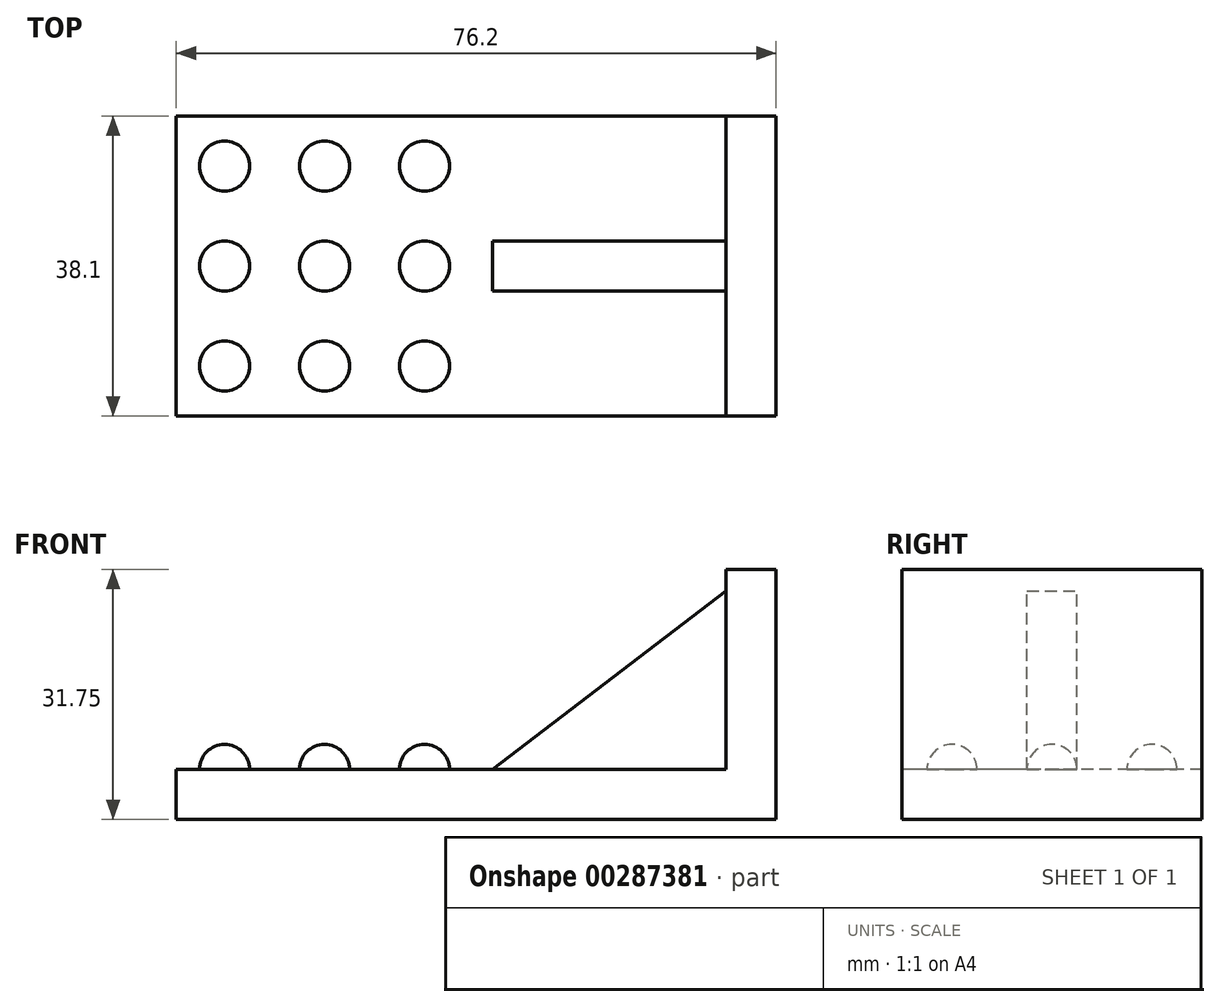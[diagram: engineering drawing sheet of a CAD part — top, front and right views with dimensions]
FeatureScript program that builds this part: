
annotation { "Feature Type Name" : "Feature", "Feature Type Description" : "" }
export const myFeature = defineFeature(function(context is Context, id is Id, definition is map)
    precondition{}
    {
        {
            var Q0;
            Q0=qCreatedBy(makeId("Top.planeOp"),FACE);
            var sketch = newSketch(context, id + "F0", { "sketchPlane" : qUnion([Q0])});
            skLineSegment(sketch, "E0.bottom", {"start": v(-38.1, 19.05) * mm, "end": v(38.1, 19.05) * mm});
            skLineSegment(sketch, "E0.top", {"start": v(-38.1, -19.05) * mm, "end": v(38.1, -19.05) * mm});
            skLineSegment(sketch, "E0.left", {"start": v(-38.1, 19.05) * mm, "end": v(-38.1, -19.05) * mm});
            skLineSegment(sketch, "E0.right", {"start": v(38.1, 19.05) * mm, "end": v(38.1, -19.05) * mm});
            skPoint(sketch, "E0.middle", {"position": v(0, 0) * mm});
            skSolve(sketch);
        }
        {
            var Q0;
            Q0 = qSketchRegion(id + "F0", true);
            extrude(context, id + "F1", {"entities" : qUnion([Q0]), "oppositeDirection" : true, "depth" : 6.35 * mm});
        }
        {
            var Q0;
            Q0=makeQuery(id+"F1.opExtrude","CAP_FACE",FACE,{"disambiguationData":[OSD([sQuery(id+"F0.wireOp",EDGE,"E0.bottom"),sQuery(id+"F0.wireOp",EDGE,"E0.top"),sQuery(id+"F0.wireOp",EDGE,"E0.left"),sQuery(id+"F0.wireOp",EDGE,"E0.right")])],"isStart":true});
            var sketch = newSketch(context, id + "F2", { "sketchPlane" : qUnion([Q0])});
            skArc(sketch, "E1", {"start": v(-31.97, 15.87) * mm, "mid": v(-35.14, 12.7) * mm, "end": v(-31.97, 9.52) * mm});
            skPoint(sketch, "E1.centerSnap0", {"position": v(-38.1, 0) * mm});
            skLineSegment(sketch, "E2", {"start": v(-31.97, 9.52) * mm, "end": v(-31.97, 15.87) * mm});
            skArc(sketch, "E3.1.0.0", {"start": v(-19.27, 15.87) * mm, "mid": v(-22.44, 12.7) * mm, "end": v(-19.27, 9.52) * mm});
            skLineSegment(sketch, "E3.1.0.1", {"start": v(-19.27, 9.52) * mm, "end": v(-19.27, 15.87) * mm});
            skArc(sketch, "E3.2.0.0", {"start": v(-6.57, 15.87) * mm, "mid": v(-9.74, 12.7) * mm, "end": v(-6.57, 9.52) * mm});
            skLineSegment(sketch, "E3.2.0.1", {"start": v(-6.57, 9.52) * mm, "end": v(-6.57, 15.87) * mm});
            skLineSegment(sketch, "E3.direction1", {"start": v(-31.97, 9.52) * mm, "end": v(-19.27, 9.52) * mm, "construction": true});
            skArc(sketch, "E4.1.0.0", {"start": v(-31.97, 3.18) * mm, "mid": v(-35.14, 0) * mm, "end": v(-31.97, -3.18) * mm});
            skLineSegment(sketch, "E4.1.0.1", {"start": v(-31.97, -3.18) * mm, "end": v(-31.97, 3.18) * mm});
            skArc(sketch, "E4.1.0.2", {"start": v(-19.27, 3.18) * mm, "mid": v(-22.44, 0) * mm, "end": v(-19.27, -3.18) * mm});
            skLineSegment(sketch, "E4.1.0.3", {"start": v(-19.27, -3.18) * mm, "end": v(-19.27, 3.18) * mm});
            skArc(sketch, "E4.1.0.4", {"start": v(-6.57, 3.18) * mm, "mid": v(-9.74, 0) * mm, "end": v(-6.57, -3.17) * mm});
            skLineSegment(sketch, "E4.1.0.5", {"start": v(-6.57, -3.17) * mm, "end": v(-6.57, 3.17) * mm});
            skArc(sketch, "E4.2.0.0", {"start": v(-31.97, -9.52) * mm, "mid": v(-35.14, -12.7) * mm, "end": v(-31.97, -15.87) * mm});
            skLineSegment(sketch, "E4.2.0.1", {"start": v(-31.97, -15.87) * mm, "end": v(-31.97, -9.52) * mm});
            skArc(sketch, "E4.2.0.2", {"start": v(-19.27, -9.52) * mm, "mid": v(-22.44, -12.7) * mm, "end": v(-19.27, -15.87) * mm});
            skLineSegment(sketch, "E4.2.0.3", {"start": v(-19.27, -15.87) * mm, "end": v(-19.27, -9.52) * mm});
            skArc(sketch, "E4.2.0.4", {"start": v(-6.57, -9.52) * mm, "mid": v(-9.74, -12.7) * mm, "end": v(-6.57, -15.87) * mm});
            skLineSegment(sketch, "E4.2.0.5", {"start": v(-6.57, -15.87) * mm, "end": v(-6.57, -9.52) * mm});
            skLineSegment(sketch, "E4.direction1", {"start": v(-31.97, 9.52) * mm, "end": v(-31.97, -3.18) * mm, "construction": true});
            skSolve(sketch);
        }
        {
            var Q0;
            Q0=makeQuery(id+"F2.imprint","IMPRINT",FACE,{"disambiguationData":[TD([[makeQuery(id+"F2.imprint","IMPRINT",EDGE,{"derivedFrom":sQuery(id+"F2.wireOp",EDGE,"E1")}),1.0]])]});
            var Q1;
            Q1=makeQuery(id+"F2.imprint","IMPRINT",FACE,{"disambiguationData":[TD([[makeQuery(id+"F2.imprint","IMPRINT",EDGE,{"derivedFrom":sQuery(id+"F2.wireOp",EDGE,"E4.1.0.0")}),1.0]])]});
            var Q2;
            Q2=makeQuery(id+"F2.imprint","IMPRINT",FACE,{"disambiguationData":[TD([[makeQuery(id+"F2.imprint","IMPRINT",EDGE,{"derivedFrom":sQuery(id+"F2.wireOp",EDGE,"E4.2.0.0")}),1.0]])]});
            var Q3;
            Q3=sQuery(id+"F2.wireOp",EDGE,"E4.1.0.1");
            revolve(context, id + "F3", {"operationType" : NewBodyOperationType.ADD, "entities" : qUnion([Q0, Q1, Q2]), "axis" : qUnion([Q3]), "revolveType" : RevolveType.FULL});
        }
        {
            var Q0;
            Q0=makeQuery(id+"F2.imprint","IMPRINT",FACE,{"disambiguationData":[TD([[makeQuery(id+"F2.imprint","IMPRINT",EDGE,{"derivedFrom":sQuery(id+"F2.wireOp",EDGE,"E3.1.0.0")}),1.0]])]});
            var Q1;
            Q1=makeQuery(id+"F2.imprint","IMPRINT",FACE,{"disambiguationData":[TD([[makeQuery(id+"F2.imprint","IMPRINT",EDGE,{"derivedFrom":sQuery(id+"F2.wireOp",EDGE,"E4.1.0.2")}),1.0]])]});
            var Q2;
            Q2=makeQuery(id+"F2.imprint","IMPRINT",FACE,{"disambiguationData":[TD([[makeQuery(id+"F2.imprint","IMPRINT",EDGE,{"derivedFrom":sQuery(id+"F2.wireOp",EDGE,"E4.2.0.2")}),1.0]])]});
            var Q3;
            Q3=sQuery(id+"F2.wireOp",EDGE,"E4.1.0.3");
            revolve(context, id + "F4", {"operationType" : NewBodyOperationType.ADD, "entities" : qUnion([Q0, Q1, Q2]), "axis" : qUnion([Q3]), "revolveType" : RevolveType.FULL});
        }
        {
            var Q0;
            Q0=makeQuery(id+"F2.imprint","IMPRINT",FACE,{"disambiguationData":[TD([[makeQuery(id+"F2.imprint","IMPRINT",EDGE,{"derivedFrom":sQuery(id+"F2.wireOp",EDGE,"E3.2.0.0")}),1.0]])]});
            var Q1;
            Q1=makeQuery(id+"F2.imprint","IMPRINT",FACE,{"disambiguationData":[TD([[makeQuery(id+"F2.imprint","IMPRINT",EDGE,{"derivedFrom":sQuery(id+"F2.wireOp",EDGE,"E4.1.0.4")}),1.0]])]});
            var Q2;
            Q2=makeQuery(id+"F2.imprint","IMPRINT",FACE,{"disambiguationData":[TD([[makeQuery(id+"F2.imprint","IMPRINT",EDGE,{"derivedFrom":sQuery(id+"F2.wireOp",EDGE,"E4.2.0.4")}),1.0]])]});
            var Q3;
            Q3=sQuery(id+"F2.wireOp",EDGE,"E4.2.0.5");
            revolve(context, id + "F5", {"operationType" : NewBodyOperationType.ADD, "entities" : qUnion([Q0, Q1, Q2]), "axis" : qUnion([Q3]), "revolveType" : RevolveType.FULL});
        }
        {
            var Q0;
            Q0=makeQuery(id+"F1.opExtrude","CAP_FACE",FACE,{"disambiguationData":[OSD([sQuery(id+"F0.wireOp",EDGE,"E0.bottom"),sQuery(id+"F0.wireOp",EDGE,"E0.top"),sQuery(id+"F0.wireOp",EDGE,"E0.left"),sQuery(id+"F0.wireOp",EDGE,"E0.right")])],"isStart":true});
            var sketch = newSketch(context, id + "F6", { "sketchPlane" : qUnion([Q0])});
            skLineSegment(sketch, "E5.bottom", {"start": v(38.1, 19.05) * mm, "end": v(31.75, 19.05) * mm});
            skLineSegment(sketch, "E5.top", {"start": v(38.1, -19.05) * mm, "end": v(31.75, -19.05) * mm});
            skLineSegment(sketch, "E5.left", {"start": v(38.1, 19.05) * mm, "end": v(38.1, -19.05) * mm});
            skLineSegment(sketch, "E5.right", {"start": v(31.75, 19.05) * mm, "end": v(31.75, -19.05) * mm});
            skSolve(sketch);
        }
        {
            var Q0;
            Q0=makeQuery(id+"F6.imprint","IMPRINT",FACE,{"disambiguationData":[TD([[makeQuery(id+"F6.imprint","IMPRINT",EDGE,{"derivedFrom":sQuery(id+"F6.wireOp",EDGE,"E5.bottom")}),-1.0]])]});
            extrude(context, id + "F7", {"entities" : qUnion([Q0]), "operationType" : NewBodyOperationType.ADD, "depth" : 25.4 * mm});
        }
        {
            var Q0;
            Q0=qCreatedBy(makeId("Front.planeOp"),FACE);
            var sketch = newSketch(context, id + "F8", { "sketchPlane" : qUnion([Q0])});
            skLineSegment(sketch, "E6", {"start": v(31.75, 22.7) * mm, "end": v(2.05, 0) * mm});
            skLineSegment(sketch, "E7", {"start": v(2.05, 0) * mm, "end": v(31.75, 0) * mm});
            skLineSegment(sketch, "E8", {"start": v(31.75, 0) * mm, "end": v(31.75, 22.7) * mm});
            skSolve(sketch);
        }
        {
            var Q0;
            Q0=makeQuery(id+"F8.imprint","IMPRINT",FACE,{"disambiguationData":[TD([[makeQuery(id+"F8.imprint","IMPRINT",EDGE,{"derivedFrom":sQuery(id+"F8.wireOp",EDGE,"E6")}),1.0]])]});
            extrude(context, id + "F9", {"entities" : qUnion([Q0]), "operationType" : NewBodyOperationType.ADD, "depth" : 6.35 * mm, "symmetric" : true});
        }
    });
